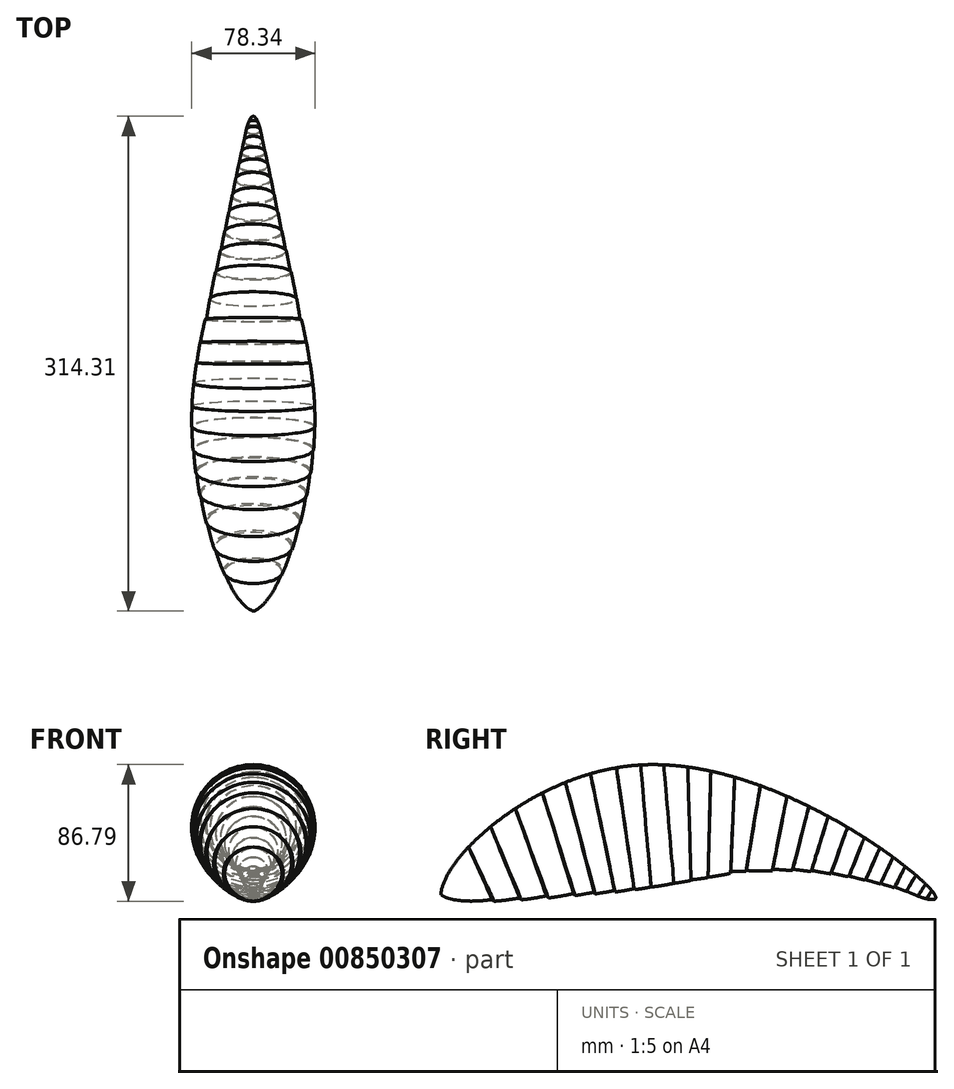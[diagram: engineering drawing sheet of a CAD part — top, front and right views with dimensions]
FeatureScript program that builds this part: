
annotation { "Feature Type Name" : "Feature", "Feature Type Description" : "" }
export const myFeature = defineFeature(function(context is Context, id is Id, definition is map)
    precondition{}
    {
        {
            var Q0;
            Q0=qCreatedBy(makeId("Right.planeOp"),FACE);
            var sketch = newSketch(context, id + "F0", { "sketchPlane" : qUnion([Q0])});
            skFitSpline(sketch, "E0", {"points": [v(0, 0) * mm, v(-187.33, 83.54) * mm, v(-312.89, -4.43) * mm, v(-94.46, 14.56) * mm, v(0, 0) * mm]});
            skLineSegment(sketch, "E1", {"start": v(-10.14, -0.42) * mm, "end": v(-6.3, 7.86) * mm});
            skLineSegment(sketch, "E2", {"start": v(-187.33, 83.54) * mm, "end": v(-187.33, 5.4) * mm});
            skLineSegment(sketch, "E3", {"start": v(-172.69, 83.62) * mm, "end": v(-172.69, 7.84) * mm});
            skLineSegment(sketch, "E4", {"start": v(-157.37, 82.2) * mm, "end": v(-157.37, 10.13) * mm});
            skLineSegment(sketch, "E5", {"start": v(-142.78, 79.6) * mm, "end": v(-142.78, 11.98) * mm});
            skLineSegment(sketch, "E6", {"start": v(-127.64, 75.74) * mm, "end": v(-127.64, 14.56) * mm});
            skLineSegment(sketch, "E7", {"start": v(-111.33, 70.4) * mm, "end": v(-111.33, 14.45) * mm});
            skLineSegment(sketch, "E8", {"start": v(-94.46, 14.56) * mm, "end": v(-94.46, 63.65) * mm});
            skLineSegment(sketch, "E9", {"start": v(-80.46, 13.79) * mm, "end": v(-80.46, 57.18) * mm});
            skLineSegment(sketch, "E10", {"start": v(-68.2, 12.46) * mm, "end": v(-68.2, 50.86) * mm});
            skLineSegment(sketch, "E11", {"start": v(-55.97, 10.56) * mm, "end": v(-55.97, 43.96) * mm});
            skLineSegment(sketch, "E12", {"start": v(-202.71, 2.67) * mm, "end": v(-202.71, 81.76) * mm});
            skLineSegment(sketch, "E13", {"start": v(-219.2, -0.39) * mm, "end": v(-219.2, 77.96) * mm});
            skLineSegment(sketch, "E14", {"start": v(-235.07, -3.33) * mm, "end": v(-235.07, 72.47) * mm});
            skLineSegment(sketch, "E15", {"start": v(-249.7, -5.94) * mm, "end": v(-249.7, 65.8) * mm});
            skLineSegment(sketch, "E16", {"start": v(-266.91, -8.66) * mm, "end": v(-266.91, 55.83) * mm});
            skLineSegment(sketch, "E17", {"start": v(-282.6, -10.43) * mm, "end": v(-282.6, 44.34) * mm});
            skLineSegment(sketch, "E18", {"start": v(-296.61, -10.74) * mm, "end": v(-296.61, 31.38) * mm});
            skLineSegment(sketch, "E19", {"start": v(-307.96, -8.49) * mm, "end": v(-307.96, 17.16) * mm});
            skLineSegment(sketch, "E20", {"start": v(-45.23, 8.47) * mm, "end": v(-45.23, 37.37) * mm});
            skLineSegment(sketch, "E21", {"start": v(-35.43, 6.23) * mm, "end": v(-35.43, 30.9) * mm});
            skLineSegment(sketch, "E22", {"start": v(-27, 4.1) * mm, "end": v(-27, 24.93) * mm});
            skLineSegment(sketch, "E23", {"start": v(-19.34, 2.05) * mm, "end": v(-19.34, 19.12) * mm});
            skLineSegment(sketch, "E24", {"start": v(-187.33, 44.47) * mm, "end": v(-202.71, 42.21) * mm});
            skLineSegment(sketch, "E25", {"start": v(-187.33, 44.47) * mm, "end": v(-172.69, 45.73) * mm});
            skLineSegment(sketch, "E26", {"start": v(-172.69, 45.73) * mm, "end": v(-157.37, 46.17) * mm});
            skLineSegment(sketch, "E27", {"start": v(-157.37, 46.17) * mm, "end": v(-142.78, 45.8) * mm});
            skLineSegment(sketch, "E28", {"start": v(-142.78, 45.8) * mm, "end": v(-127.64, 45.15) * mm});
            skLineSegment(sketch, "E29", {"start": v(-127.64, 45.15) * mm, "end": v(-111.33, 42.42) * mm});
            skLineSegment(sketch, "E30", {"start": v(-111.33, 42.42) * mm, "end": v(-94.46, 39.1) * mm});
            skLineSegment(sketch, "E31", {"start": v(-94.46, 39.1) * mm, "end": v(-80.46, 35.48) * mm});
            skLineSegment(sketch, "E32", {"start": v(-80.46, 35.48) * mm, "end": v(-68.2, 31.66) * mm});
            skLineSegment(sketch, "E33", {"start": v(-68.2, 31.66) * mm, "end": v(-55.97, 27.26) * mm});
            skLineSegment(sketch, "E34", {"start": v(-55.97, 27.26) * mm, "end": v(-45.23, 22.92) * mm});
            skLineSegment(sketch, "E35", {"start": v(-45.23, 22.92) * mm, "end": v(-35.43, 18.56) * mm});
            skLineSegment(sketch, "E36", {"start": v(-35.43, 18.56) * mm, "end": v(-27, 14.52) * mm});
            skLineSegment(sketch, "E37", {"start": v(-27, 14.52) * mm, "end": v(-19.34, 10.58) * mm});
            skLineSegment(sketch, "E38", {"start": v(-202.71, 42.21) * mm, "end": v(-219.2, 38.79) * mm});
            skLineSegment(sketch, "E39", {"start": v(-219.2, 38.79) * mm, "end": v(-235.07, 34.57) * mm});
            skLineSegment(sketch, "E40", {"start": v(-235.07, 34.57) * mm, "end": v(-249.7, 29.93) * mm});
            skLineSegment(sketch, "E41", {"start": v(-249.7, 29.93) * mm, "end": v(-266.91, 23.58) * mm});
            skLineSegment(sketch, "E42", {"start": v(-266.91, 23.58) * mm, "end": v(-282.6, 16.95) * mm});
            skLineSegment(sketch, "E43", {"start": v(-282.6, 16.95) * mm, "end": v(-296.61, 10.32) * mm});
            skLineSegment(sketch, "E44", {"start": v(-296.61, 10.32) * mm, "end": v(-307.96, 4.34) * mm});
            skLineSegment(sketch, "E45", {"start": v(-12.53, 13.53) * mm, "end": v(-14.38, 0.7) * mm});
            skLineSegment(sketch, "E46", {"start": v(-2.46, 3.75) * mm, "end": v(-5.95, -1.4) * mm});
            skLineSegment(sketch, "E47", {"start": v(-19.34, 10.58) * mm, "end": v(-13.45, 7.11) * mm});
            skLineSegment(sketch, "E48", {"start": v(-13.45, 7.11) * mm, "end": v(-8.22, 3.72) * mm});
            skLineSegment(sketch, "E49", {"start": v(-8.22, 3.72) * mm, "end": v(-4.2, 1.18) * mm});
            skLineSegment(sketch, "E50", {"start": v(-4.2, 1.18) * mm, "end": v(0, -1.27) * mm});
            skLineSegment(sketch, "E51", {"start": v(-307.96, 4.34) * mm, "end": v(-314.17, 1.07) * mm});
            skSolve(sketch);
        }
        {
            var Q0;
            {var subQ5=sQuery(id+"F0.wireOp",EDGE,"E24");Q0=makeQuery(id+"F0.imprint","IMPRINT",FACE,{"disambiguationData":[TD([[makeQuery(id+"F0.imprint","IMPRINT",EDGE,{"derivedFrom":subQ5}),-1.0]])]});}
            var Q1;
            Q1=sQuery(id+"F0.wireOp",EDGE,"E24");
            revolve(context, id + "F1", {"surfaceOperationType" : NewSurfaceOperationType.NEW, "entities" : qUnion([Q0]), "axis" : qUnion([Q1]), "revolveType" : RevolveType.FULL});
        }
        {
            var Q0;
            {var subQ5=sQuery(id+"F0.wireOp",EDGE,"E38");Q0=makeQuery(id+"F0.imprint","IMPRINT",FACE,{"disambiguationData":[TD([[makeQuery(id+"F0.imprint","IMPRINT",EDGE,{"derivedFrom":subQ5}),-1.0]])]});}
            var Q1;
            Q1=sQuery(id+"F0.wireOp",EDGE,"E38");
            revolve(context, id + "F2", {"operationType" : NewBodyOperationType.ADD, "surfaceOperationType" : NewSurfaceOperationType.NEW, "entities" : qUnion([Q0]), "axis" : qUnion([Q1]), "revolveType" : RevolveType.FULL});
        }
        {
            var Q0;
            {var subQ5=sQuery(id+"F0.wireOp",EDGE,"E39");Q0=makeQuery(id+"F0.imprint","IMPRINT",FACE,{"disambiguationData":[TD([[makeQuery(id+"F0.imprint","IMPRINT",EDGE,{"derivedFrom":subQ5}),-1.0]])]});}
            var Q1;
            Q1=sQuery(id+"F0.wireOp",EDGE,"E39");
            revolve(context, id + "F3", {"operationType" : NewBodyOperationType.ADD, "surfaceOperationType" : NewSurfaceOperationType.NEW, "entities" : qUnion([Q0]), "axis" : qUnion([Q1]), "revolveType" : RevolveType.FULL});
        }
        {
            var Q0;
            {var subQ5=sQuery(id+"F0.wireOp",EDGE,"E40");Q0=makeQuery(id+"F0.imprint","IMPRINT",FACE,{"disambiguationData":[TD([[makeQuery(id+"F0.imprint","IMPRINT",EDGE,{"derivedFrom":subQ5}),-1.0]])]});}
            var Q1;
            Q1=sQuery(id+"F0.wireOp",EDGE,"E40");
            revolve(context, id + "F4", {"operationType" : NewBodyOperationType.ADD, "surfaceOperationType" : NewSurfaceOperationType.NEW, "entities" : qUnion([Q0]), "axis" : qUnion([Q1]), "revolveType" : RevolveType.FULL});
        }
        {
            var Q0;
            {var subQ5=sQuery(id+"F0.wireOp",EDGE,"E41");Q0=makeQuery(id+"F0.imprint","IMPRINT",FACE,{"disambiguationData":[TD([[makeQuery(id+"F0.imprint","IMPRINT",EDGE,{"derivedFrom":subQ5}),-1.0]])]});}
            var Q1;
            Q1=sQuery(id+"F0.wireOp",EDGE,"E41");
            revolve(context, id + "F5", {"operationType" : NewBodyOperationType.ADD, "surfaceOperationType" : NewSurfaceOperationType.NEW, "entities" : qUnion([Q0]), "axis" : qUnion([Q1]), "revolveType" : RevolveType.FULL});
        }
        {
            var Q0;
            {var subQ5=sQuery(id+"F0.wireOp",EDGE,"E42");Q0=makeQuery(id+"F0.imprint","IMPRINT",FACE,{"disambiguationData":[TD([[makeQuery(id+"F0.imprint","IMPRINT",EDGE,{"derivedFrom":subQ5}),-1.0]])]});}
            var Q1;
            Q1=sQuery(id+"F0.wireOp",EDGE,"E42");
            revolve(context, id + "F6", {"operationType" : NewBodyOperationType.ADD, "surfaceOperationType" : NewSurfaceOperationType.NEW, "entities" : qUnion([Q0]), "axis" : qUnion([Q1]), "revolveType" : RevolveType.FULL});
        }
        {
            var Q0;
            {var subQ5=sQuery(id+"F0.wireOp",EDGE,"E43");Q0=makeQuery(id+"F0.imprint","IMPRINT",FACE,{"disambiguationData":[TD([[makeQuery(id+"F0.imprint","IMPRINT",EDGE,{"derivedFrom":subQ5}),-1.0]])]});}
            var Q1;
            Q1=sQuery(id+"F0.wireOp",EDGE,"E43");
            revolve(context, id + "F7", {"operationType" : NewBodyOperationType.ADD, "surfaceOperationType" : NewSurfaceOperationType.NEW, "entities" : qUnion([Q0]), "axis" : qUnion([Q1]), "revolveType" : RevolveType.FULL});
        }
        {
            var Q0;
            {var subQ5=sQuery(id+"F0.wireOp",EDGE,"E44");Q0=makeQuery(id+"F0.imprint","IMPRINT",FACE,{"disambiguationData":[TD([[makeQuery(id+"F0.imprint","IMPRINT",EDGE,{"derivedFrom":subQ5}),-1.0]])]});}
            var Q1;
            Q1=sQuery(id+"F0.wireOp",EDGE,"E44");
            revolve(context, id + "F8", {"operationType" : NewBodyOperationType.ADD, "surfaceOperationType" : NewSurfaceOperationType.NEW, "entities" : qUnion([Q0]), "axis" : qUnion([Q1]), "revolveType" : RevolveType.FULL});
        }
        {
            var Q0;
            {var subQ5=sQuery(id+"F0.wireOp",EDGE,"E25");Q0=makeQuery(id+"F0.imprint","IMPRINT",FACE,{"disambiguationData":[TD([[makeQuery(id+"F0.imprint","IMPRINT",EDGE,{"derivedFrom":subQ5}),1.0]])]});}
            var Q1;
            Q1=sQuery(id+"F0.wireOp",EDGE,"E25");
            revolve(context, id + "F9", {"operationType" : NewBodyOperationType.ADD, "surfaceOperationType" : NewSurfaceOperationType.NEW, "entities" : qUnion([Q0]), "axis" : qUnion([Q1]), "revolveType" : RevolveType.FULL});
        }
        {
            var Q0;
            {var subQ5=sQuery(id+"F0.wireOp",EDGE,"E26");Q0=makeQuery(id+"F0.imprint","IMPRINT",FACE,{"disambiguationData":[TD([[makeQuery(id+"F0.imprint","IMPRINT",EDGE,{"derivedFrom":subQ5}),1.0]])]});}
            var Q1;
            Q1=sQuery(id+"F0.wireOp",EDGE,"E26");
            revolve(context, id + "F10", {"operationType" : NewBodyOperationType.ADD, "surfaceOperationType" : NewSurfaceOperationType.NEW, "entities" : qUnion([Q0]), "axis" : qUnion([Q1]), "revolveType" : RevolveType.FULL});
        }
        {
            var Q0;
            {var subQ5=sQuery(id+"F0.wireOp",EDGE,"E27");Q0=makeQuery(id+"F0.imprint","IMPRINT",FACE,{"disambiguationData":[TD([[makeQuery(id+"F0.imprint","IMPRINT",EDGE,{"derivedFrom":subQ5}),1.0]])]});}
            var Q1;
            Q1=sQuery(id+"F0.wireOp",EDGE,"E27");
            revolve(context, id + "F11", {"operationType" : NewBodyOperationType.ADD, "surfaceOperationType" : NewSurfaceOperationType.NEW, "entities" : qUnion([Q0]), "axis" : qUnion([Q1]), "revolveType" : RevolveType.FULL});
        }
        {
            var Q0;
            {var subQ5=sQuery(id+"F0.wireOp",EDGE,"E28");Q0=makeQuery(id+"F0.imprint","IMPRINT",FACE,{"disambiguationData":[TD([[makeQuery(id+"F0.imprint","IMPRINT",EDGE,{"derivedFrom":subQ5}),1.0]])]});}
            var Q1;
            Q1=sQuery(id+"F0.wireOp",EDGE,"E28");
            revolve(context, id + "F12", {"operationType" : NewBodyOperationType.ADD, "surfaceOperationType" : NewSurfaceOperationType.NEW, "entities" : qUnion([Q0]), "axis" : qUnion([Q1]), "revolveType" : RevolveType.FULL});
        }
        {
            var Q0;
            {var subQ5=sQuery(id+"F0.wireOp",EDGE,"E29");Q0=makeQuery(id+"F0.imprint","IMPRINT",FACE,{"disambiguationData":[TD([[makeQuery(id+"F0.imprint","IMPRINT",EDGE,{"derivedFrom":subQ5}),1.0]])]});}
            var Q1;
            Q1=sQuery(id+"F0.wireOp",EDGE,"E29");
            revolve(context, id + "F13", {"operationType" : NewBodyOperationType.ADD, "surfaceOperationType" : NewSurfaceOperationType.NEW, "entities" : qUnion([Q0]), "axis" : qUnion([Q1]), "revolveType" : RevolveType.FULL});
        }
        {
            var Q0;
            {var subQ5=sQuery(id+"F0.wireOp",EDGE,"E30");Q0=makeQuery(id+"F0.imprint","IMPRINT",FACE,{"disambiguationData":[TD([[makeQuery(id+"F0.imprint","IMPRINT",EDGE,{"derivedFrom":subQ5}),1.0]])]});}
            var Q1;
            Q1=sQuery(id+"F0.wireOp",EDGE,"E30");
            revolve(context, id + "F14", {"operationType" : NewBodyOperationType.ADD, "surfaceOperationType" : NewSurfaceOperationType.NEW, "entities" : qUnion([Q0]), "axis" : qUnion([Q1]), "revolveType" : RevolveType.FULL});
        }
        {
            var Q0;
            {var subQ5=sQuery(id+"F0.wireOp",EDGE,"E31");Q0=makeQuery(id+"F0.imprint","IMPRINT",FACE,{"disambiguationData":[TD([[makeQuery(id+"F0.imprint","IMPRINT",EDGE,{"derivedFrom":subQ5}),1.0]])]});}
            var Q1;
            Q1=sQuery(id+"F0.wireOp",EDGE,"E31");
            revolve(context, id + "F15", {"operationType" : NewBodyOperationType.ADD, "surfaceOperationType" : NewSurfaceOperationType.NEW, "entities" : qUnion([Q0]), "axis" : qUnion([Q1]), "revolveType" : RevolveType.FULL});
        }
        {
            var Q0;
            {var subQ5=sQuery(id+"F0.wireOp",EDGE,"E32");Q0=makeQuery(id+"F0.imprint","IMPRINT",FACE,{"disambiguationData":[TD([[makeQuery(id+"F0.imprint","IMPRINT",EDGE,{"derivedFrom":subQ5}),1.0]])]});}
            var Q1;
            Q1=sQuery(id+"F0.wireOp",EDGE,"E32");
            revolve(context, id + "F16", {"operationType" : NewBodyOperationType.ADD, "surfaceOperationType" : NewSurfaceOperationType.NEW, "entities" : qUnion([Q0]), "axis" : qUnion([Q1]), "revolveType" : RevolveType.FULL});
        }
        {
            var Q0;
            {var subQ5=sQuery(id+"F0.wireOp",EDGE,"E33");Q0=makeQuery(id+"F0.imprint","IMPRINT",FACE,{"disambiguationData":[TD([[makeQuery(id+"F0.imprint","IMPRINT",EDGE,{"derivedFrom":subQ5}),1.0]])]});}
            var Q1;
            Q1=sQuery(id+"F0.wireOp",EDGE,"E33");
            revolve(context, id + "F17", {"operationType" : NewBodyOperationType.ADD, "surfaceOperationType" : NewSurfaceOperationType.NEW, "entities" : qUnion([Q0]), "axis" : qUnion([Q1]), "revolveType" : RevolveType.FULL});
        }
        {
            var Q0;
            {var subQ5=sQuery(id+"F0.wireOp",EDGE,"E34");Q0=makeQuery(id+"F0.imprint","IMPRINT",FACE,{"disambiguationData":[TD([[makeQuery(id+"F0.imprint","IMPRINT",EDGE,{"derivedFrom":subQ5}),1.0]])]});}
            var Q1;
            Q1=sQuery(id+"F0.wireOp",EDGE,"E34");
            revolve(context, id + "F18", {"operationType" : NewBodyOperationType.ADD, "surfaceOperationType" : NewSurfaceOperationType.NEW, "entities" : qUnion([Q0]), "axis" : qUnion([Q1]), "revolveType" : RevolveType.FULL});
        }
        {
            var Q0;
            {var subQ5=sQuery(id+"F0.wireOp",EDGE,"E35");Q0=makeQuery(id+"F0.imprint","IMPRINT",FACE,{"disambiguationData":[TD([[makeQuery(id+"F0.imprint","IMPRINT",EDGE,{"derivedFrom":subQ5}),1.0]])]});}
            var Q1;
            Q1=sQuery(id+"F0.wireOp",EDGE,"E35");
            revolve(context, id + "F19", {"operationType" : NewBodyOperationType.ADD, "surfaceOperationType" : NewSurfaceOperationType.NEW, "entities" : qUnion([Q0]), "axis" : qUnion([Q1]), "revolveType" : RevolveType.FULL});
        }
        {
            var Q0;
            {var subQ5=sQuery(id+"F0.wireOp",EDGE,"E36");Q0=makeQuery(id+"F0.imprint","IMPRINT",FACE,{"disambiguationData":[TD([[makeQuery(id+"F0.imprint","IMPRINT",EDGE,{"derivedFrom":subQ5}),1.0]])]});}
            var Q1;
            Q1=sQuery(id+"F0.wireOp",EDGE,"E36");
            revolve(context, id + "F20", {"operationType" : NewBodyOperationType.ADD, "surfaceOperationType" : NewSurfaceOperationType.NEW, "entities" : qUnion([Q0]), "axis" : qUnion([Q1]), "revolveType" : RevolveType.FULL});
        }
        {
            var Q0;
            {var subQ5=sQuery(id+"F0.wireOp",EDGE,"E37");Q0=makeQuery(id+"F0.imprint","IMPRINT",FACE,{"disambiguationData":[TD([[makeQuery(id+"F0.imprint","IMPRINT",EDGE,{"derivedFrom":subQ5}),1.0]])]});}
            var Q1;
            Q1=sQuery(id+"F0.wireOp",EDGE,"E37");
            revolve(context, id + "F21", {"operationType" : NewBodyOperationType.ADD, "surfaceOperationType" : NewSurfaceOperationType.NEW, "entities" : qUnion([Q0]), "axis" : qUnion([Q1]), "revolveType" : RevolveType.FULL});
        }
        {
            var Q0;
            {var subQ5=sQuery(id+"F0.wireOp",EDGE,"E47");Q0=makeQuery(id+"F0.imprint","IMPRINT",FACE,{"disambiguationData":[TD([[makeQuery(id+"F0.imprint","IMPRINT",EDGE,{"derivedFrom":subQ5}),1.0]])]});}
            var Q1;
            Q1=sQuery(id+"F0.wireOp",EDGE,"E47");
            revolve(context, id + "F22", {"operationType" : NewBodyOperationType.ADD, "surfaceOperationType" : NewSurfaceOperationType.NEW, "entities" : qUnion([Q0]), "axis" : qUnion([Q1]), "revolveType" : RevolveType.FULL});
        }
        {
            var Q0;
            {var subQ5=sQuery(id+"F0.wireOp",EDGE,"E48");Q0=makeQuery(id+"F0.imprint","IMPRINT",FACE,{"disambiguationData":[TD([[makeQuery(id+"F0.imprint","IMPRINT",EDGE,{"derivedFrom":subQ5}),1.0]])]});}
            var Q1;
            Q1=sQuery(id+"F0.wireOp",EDGE,"E48");
            revolve(context, id + "F23", {"operationType" : NewBodyOperationType.ADD, "surfaceOperationType" : NewSurfaceOperationType.NEW, "entities" : qUnion([Q0]), "axis" : qUnion([Q1]), "revolveType" : RevolveType.FULL});
        }
        {
            var Q0;
            {var subQ5=sQuery(id+"F0.wireOp",EDGE,"E49");Q0=makeQuery(id+"F0.imprint","IMPRINT",FACE,{"disambiguationData":[TD([[makeQuery(id+"F0.imprint","IMPRINT",EDGE,{"derivedFrom":subQ5}),1.0]])]});}
            var Q1;
            Q1=sQuery(id+"F0.wireOp",EDGE,"E49");
            revolve(context, id + "F24", {"operationType" : NewBodyOperationType.ADD, "surfaceOperationType" : NewSurfaceOperationType.NEW, "entities" : qUnion([Q0]), "axis" : qUnion([Q1]), "revolveType" : RevolveType.FULL});
        }
        {
            var Q0;
            {var subQ3=sQuery(id+"F0.wireOp",EDGE,"E50");Q0=makeQuery(id+"F0.imprint","IMPRINT",FACE,{"disambiguationData":[TD([[makeQuery(id+"F0.imprint","IMPRINT",EDGE,{"derivedFrom":subQ3}),1.0]])]});}
            var Q1;
            Q1=sQuery(id+"F0.wireOp",EDGE,"E50");
            revolve(context, id + "F25", {"operationType" : NewBodyOperationType.ADD, "surfaceOperationType" : NewSurfaceOperationType.NEW, "entities" : qUnion([Q0]), "axis" : qUnion([Q1]), "revolveType" : RevolveType.FULL});
        }
        {
            var Q0;
            {var subQ3=sQuery(id+"F0.wireOp",EDGE,"E51");Q0=makeQuery(id+"F0.imprint","IMPRINT",FACE,{"disambiguationData":[TD([[makeQuery(id+"F0.imprint","IMPRINT",EDGE,{"derivedFrom":subQ3}),-1.0]])]});}
            var Q1;
            Q1=sQuery(id+"F0.wireOp",EDGE,"E51");
            revolve(context, id + "F26", {"operationType" : NewBodyOperationType.ADD, "surfaceOperationType" : NewSurfaceOperationType.NEW, "entities" : qUnion([Q0]), "axis" : qUnion([Q1]), "revolveType" : RevolveType.FULL});
        }
    });
